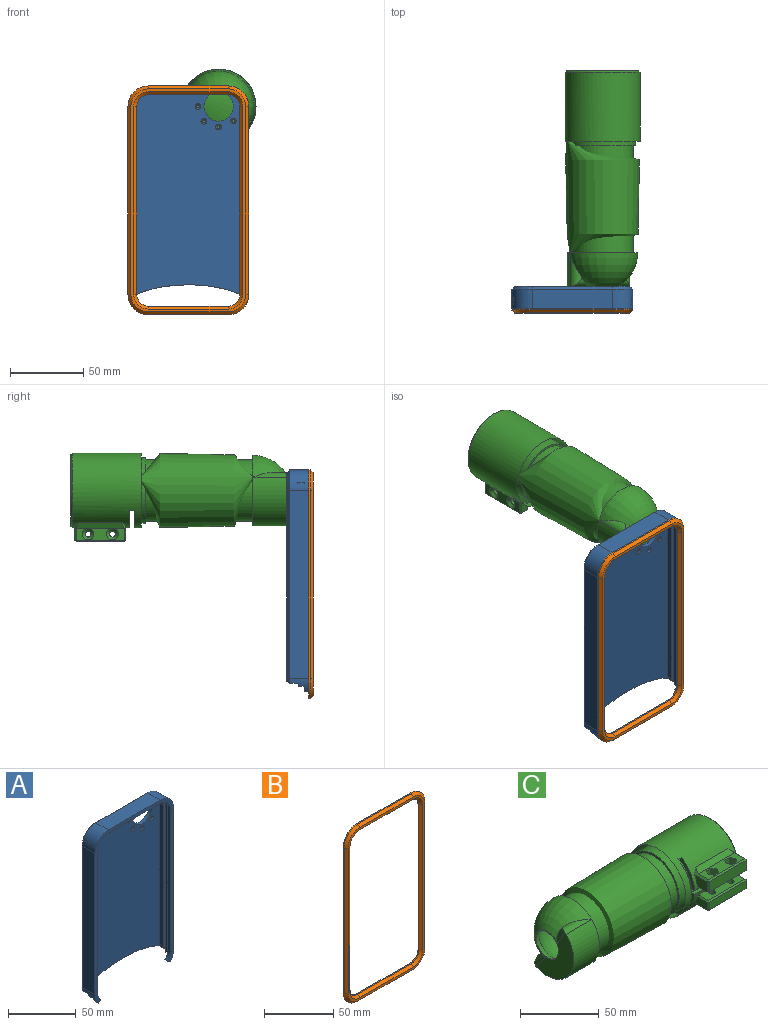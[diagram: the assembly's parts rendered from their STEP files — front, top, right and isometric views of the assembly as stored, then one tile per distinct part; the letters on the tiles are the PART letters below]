
ASSEMBLY  parts=3 mates=1
PART A: 50 faces, bbox 82.3x15x151.3 mm
  f0: cylinder r=14mm len=13mm, axis (0,1,0), area 73mm2, adj f6,f13,f15,f25,f34,f37,f38,f45
  f1: cylinder r=14mm len=13mm, axis (0,1,0), area 73mm2, adj f5,f14,f15,f17,f31,f36,f38,f39
  f2: plane 142.06x78.25mm, normal (0,1,0), area 10255.9mm2, adj f21,f22,f23,f24,f26,f38,f39,f40
  f3: cylinder r=11mm len=4.5mm, axis (0,1,0), area 6.8mm2, adj f16,f27,f35,f38
  f4: cylinder r=11mm len=4.5mm, axis (0,1,0), area 6.8mm2, adj f16,f29,f30,f38
  f5: plane 138.8x4.5mm, normal (-1,0,0), area 623.2mm2, adj f1,f30,f31,f32,f36,f38
  f6: plane 138.8x4.5mm, normal (1,0,0), area 623.2mm2, adj f0,f33,f34,f35,f37,f38
  f7: cylinder r=11mm len=7.84mm, axis (0,1,0), area 26.2mm2, adj f9,f13,f15,f34
  f8: cylinder r=11mm len=7.84mm, axis (0,1,0), area 26.2mm2, adj f12,f14,f15,f31
  f9: plane 128x3mm, normal (1,0,0), area 384mm2, adj f7,f10,f15,f34
  f10: cylinder r=11mm len=12mm, axis (0,1,0), area 182.4mm2, adj f9,f15,f16,f27,f28,f33,f34,f35
  f11: cylinder r=11mm len=12mm, axis (0,1,0), area 182.4mm2, adj f12,f15,f16,f28,f29,f30,f31,f32
  f12: plane 128x3mm, normal (-1,0,0), area 384mm2, adj f8,f11,f15,f31
  f13: extruded ~3x2.77mm, area 9.4mm2, adj f0,f7,f15,f34
  f14: extruded ~3x2.77mm, area 9.4mm2, adj f1,f8,f15,f31
  f15: plane 151.28x82.25mm, normal (0,-1,0), area 1105.1mm2, adj f0,f1,f7,f8,f9,f10,f11,f12
  f16: plane 140.5x76.25mm, normal (0,-1,0), area 9868.2mm2, adj f3,f4,f10,f11,f26,f27,f28,f29
  f17: plane 128x13mm, normal (1,0,0), area 1664mm2, adj f1,f15,f18,f40
  f18: cylinder r=14mm len=14mm, axis (0,1,0), area 285.9mm2, adj f15,f17,f19,f41
  f19: plane 54.25x13mm, normal (0,0,1), area 705.2mm2, adj f15,f18,f20,f42
  f20: cylinder r=14mm len=14mm, axis (0,1,0), area 285.9mm2, adj f15,f19,f25,f43
  f21: cylinder r=1mm len=2mm, axis (0,1,0), area 12.6mm2, adj f2,f49
  f22: cylinder r=1mm len=2mm, axis (0,1,0), area 12.6mm2, adj f2,f48
  f23: cylinder r=1mm len=2mm, axis (0,1,0), area 12.6mm2, adj f2,f47
  f24: cylinder r=1mm len=2mm, axis (0,1,0), area 12.6mm2, adj f2,f46
  f25: plane 128x13mm, normal (-1,0,0), area 1664mm2, adj f0,f15,f20,f44
  f26: cylinder r=10mm len=20mm, axis (0,1,0), area 188.5mm2, adj f2,f16
  f27: plane 128x4.5mm, normal (1,0,0), area 576mm2, adj f3,f10,f16,f35
  f28: plane 54.25x12mm, normal (0,0,-1), area 651mm2, adj f10,f11,f15,f16
  f29: plane 128x4.5mm, normal (-1,0,0), area 576mm2, adj f4,f11,f16,f30
  f30: plane 136.07x3.24mm, normal (0,-1,0), area 256.4mm2, adj f4,f5,f11,f29,f32,f38
  f31: plane 142.59x5.16mm, normal (0,1,0), area 276.4mm2, adj f1,f5,f8,f11,f12,f14,f32
  f32: plane 4.5x3.24mm, normal (0,0,-1), area 14.6mm2, adj f5,f11,f30,f31
  f33: plane 4.5x3.24mm, normal (0,0,-1), area 14.6mm2, adj f6,f10,f34,f35
  f34: plane 142.59x5.16mm, normal (0,1,0), area 276.4mm2, adj f0,f6,f7,f9,f10,f13,f33
  f35: plane 136.07x3.24mm, normal (0,-1,0), area 256.4mm2, adj f3,f6,f10,f27,f33,f38
  f36: plane 2.73x0.73mm, normal (0,1,0), area 1.1mm2, adj f1,f5,f38
  f37: plane 2.73x0.73mm, normal (0,1,0), area 1.1mm2, adj f0,f6,f38
  f38: extruded ~81.46x9.82mm, area 280.9mm2, adj f0,f1,f2,f3,f4,f5,f6,f16
  f39: cone r=14mm half-angle=45deg, axis (0,-1,0), area 7.6mm2, adj f1,f2,f38,f40
  f40: plane 128x2mm, normal (0.71,0.71,0), area 362mm2, adj f2,f17,f39,f41
  f41: cone r=14mm half-angle=45deg, axis (0,-1,0), area 57.8mm2, adj f2,f18,f40,f42
  f42: plane 54.25x2mm, normal (0,0.71,0.71), area 153.4mm2, adj f2,f19,f41,f43
  f43: cone r=14mm half-angle=45deg, axis (0,-1,0), area 57.8mm2, adj f2,f20,f42,f44
  f44: plane 128x2mm, normal (-0.71,0.71,0), area 362mm2, adj f2,f25,f43,f45
  f45: cone r=14mm half-angle=45deg, axis (0,-1,0), area 7.6mm2, adj f0,f2,f38,f44
  f46: cone r=1mm half-angle=45deg, axis (0,-1,0), area 13.3mm2, adj f16,f24
  f47: cone r=1mm half-angle=45deg, axis (0,-1,0), area 13.3mm2, adj f16,f23
  f48: cone r=1mm half-angle=45deg, axis (0,-1,0), area 13.3mm2, adj f16,f22
  f49: cone r=1mm half-angle=45deg, axis (0,-1,0), area 13.3mm2, adj f16,f21
PART B: 34 faces, bbox 82.3x3x156 mm
  f0: cylinder r=8mm len=8mm, axis (0,1,0), area 12.6mm2, adj f1,f15,f17,f26
  f1: plane 128x1mm, normal (-1,0,0), area 128mm2, adj f0,f2,f17,f28
  f2: cylinder r=8mm len=8mm, axis (0,1,0), area 12.6mm2, adj f1,f3,f17,f30
  f3: plane 54.25x1mm, normal (0,0,1), area 54.2mm2, adj f2,f4,f17,f32
  f4: cylinder r=8mm len=8mm, axis (0,1,0), area 12.6mm2, adj f3,f5,f17,f33
  f5: plane 128x1mm, normal (1,0,0), area 128mm2, adj f4,f6,f17,f31
  f6: cylinder r=8mm len=8mm, axis (0,1,0), area 12.6mm2, adj f5,f15,f17,f29
  f7: cylinder r=14mm len=14mm, axis (0,1,0), area 22mm2, adj f8,f14,f17,f23
  f8: plane 54.25x1mm, normal (0,0,-1), area 54.2mm2, adj f7,f9,f17,f25
  f9: cylinder r=14mm len=14mm, axis (0,1,0), area 22mm2, adj f8,f10,f17,f24
  f10: plane 128x1mm, normal (1,0,0), area 128mm2, adj f9,f11,f17,f22
  f11: cylinder r=14mm len=14mm, axis (0,1,0), area 22mm2, adj f10,f12,f17,f20
  f12: plane 54.25x1mm, normal (0,0,1), area 54.2mm2, adj f11,f13,f17,f18
  f13: cylinder r=14mm len=14mm, axis (0,1,0), area 22mm2, adj f12,f14,f17,f19
  f14: plane 128x1mm, normal (-1,0,0), area 128mm2, adj f7,f13,f17,f21
  f15: plane 54.25x1mm, normal (0,0,-1), area 54.2mm2, adj f0,f6,f17,f27
  f16: plane 152x78.25mm, normal (0,-1,0), area 867.2mm2, adj f18,f19,f20,f21,f22,f23,f24,f25
  f17: plane 156x82.25mm, normal (0,1,0), area 2601.7mm2, adj f0,f1,f2,f3,f4,f5,f6,f7
  f18: plane 54.25x2mm, normal (0,-0.71,0.71), area 153.4mm2, adj f12,f16,f19,f20
  f19: cone r=12mm half-angle=45deg, axis (0,1,0), area 57.8mm2, adj f13,f16,f18,f21
  f20: cone r=12mm half-angle=45deg, axis (0,1,0), area 57.8mm2, adj f11,f16,f18,f22
  f21: plane 128x2mm, normal (-0.71,-0.71,0), area 362mm2, adj f14,f16,f19,f23
  f22: plane 128x2mm, normal (0.71,-0.71,0), area 362mm2, adj f10,f16,f20,f24
  f23: cone r=12mm half-angle=45deg, axis (0,1,0), area 57.8mm2, adj f7,f16,f21,f25
  f24: cone r=12mm half-angle=45deg, axis (0,1,0), area 57.8mm2, adj f9,f16,f22,f25
  f25: plane 54.25x2mm, normal (0,-0.71,-0.71), area 153.4mm2, adj f8,f16,f23,f24
  f26: cone r=8mm half-angle=45deg, axis (0,-1,0), area 40mm2, adj f0,f16,f27,f28
  f27: plane 54.25x2mm, normal (0,-0.71,-0.71), area 153.4mm2, adj f15,f16,f26,f29
  f28: plane 128x2mm, normal (-0.71,-0.71,0), area 362mm2, adj f1,f16,f26,f30
  f29: cone r=8mm half-angle=45deg, axis (0,-1,0), area 40mm2, adj f6,f16,f27,f31
  f30: cone r=8mm half-angle=45deg, axis (0,-1,0), area 40mm2, adj f2,f16,f28,f32
  f31: plane 128x2mm, normal (0.71,-0.71,0), area 362mm2, adj f5,f16,f29,f33
  f32: plane 54.25x2mm, normal (0,-0.71,0.71), area 153.4mm2, adj f3,f16,f30,f33
  f33: cone r=8mm half-angle=45deg, axis (0,-1,0), area 40mm2, adj f4,f16,f31,f32
PART C: 82 faces, bbox 147.1x60.6x51.1 mm
  f0: cylinder r=2mm len=4.8mm, axis (0,0,1), area 60.3mm2, adj f23,f69
  f1: cylinder r=2mm len=4.8mm, axis (0,0,1), area 60.3mm2, adj f23,f62
  f2: cylinder r=22.5mm len=51mm, axis (-1,0,0), area 6918.2mm2, adj f4,f10,f12,f13,f14,f15,f16,f17
  f3: cylinder r=25.5mm len=51mm, axis (-1,0,0), area 6443.8mm2, adj f11,f12,f13,f14,f15,f16,f17,f18
  f4: plane 49x48.96mm, normal (1,0,0), area 289.2mm2, adj f2,f12,f18,f29
  f5: revolved ~47.66x44.22mm, area 1755.3mm2, adj f6,f11,f75,f76,f77,f78,f79,f80
  f6: plane 41.7x34.84mm, normal (-1,0,0), area 669.8mm2, adj f5,f7,f74,f77,f78,f79,f80
  f7: cylinder r=10mm len=20mm, axis (-1,0,0), area 12.3mm2, adj f6,f81
  f8: revolved ~42x42mm, area 2399.2mm2, adj f9,f81
  f9: cylinder r=21mm len=73mm, axis (-1,0,0), area 9632.1mm2, adj f8,f10
  f10: plane 45x45mm, normal (1,0,0), area 205mm2, adj f2,f9
  f11: cone r=24mm half-angle=1.1deg, axis (1,0,0), area 11821mm2, adj f3,f5,f74
  f12: plane 40.01x3.01mm, normal (0,0,-1), area 119.8mm2, adj f2,f3,f4,f13,f29
  f13: plane 20x18.82mm, normal (-1,0,0), area 75.9mm2, adj f2,f3,f12,f14
  f14: plane 7.08x3mm, normal (0,0,-1), area 21.2mm2, adj f2,f3,f13,f15
  f15: plane 43x18.87mm, normal (1,0,0), area 160.7mm2, adj f2,f3,f14,f16
  f16: plane 7.08x3mm, normal (0,0,1), area 21.2mm2, adj f2,f3,f15,f17
  f17: plane 20x18.82mm, normal (-1,0,0), area 75.9mm2, adj f2,f3,f16,f18
  f18: plane 40.01x3.01mm, normal (0,0,1), area 119.8mm2, adj f2,f3,f4,f17,f29
  f19: plane 33x8mm, normal (0,-1,0), area 264mm2, adj f45,f46,f50,f51
  f20: plane 11.24x8mm, normal (-1,0,0), area 78mm2, adj f3,f44,f50,f53
  f21: plane 33x9.08mm, normal (0,0,1), area 214.9mm2, adj f42,f44,f45,f56,f57,f58,f59,f60
  f22: plane 11.24x8mm, normal (1,0,0), area 78mm2, adj f3,f42,f46,f47
  f23: plane 33x8.62mm, normal (0,0,-1), area 259.4mm2, adj f0,f1,f3,f47,f51,f53
  f24: plane 33x6mm, normal (0,-1,0), area 198mm2, adj f33,f34,f38,f39
  f25: plane 33x8.42mm, normal (0,0,-1), area 177.2mm2, adj f30,f34,f35,f71,f72,f73
  f26: plane 10.76x6mm, normal (-1,0,0), area 58.2mm2, adj f3,f35,f39,f41
  f27: plane 33x8.74mm, normal (0,0,1), area 263.3mm2, adj f3,f32,f38,f41,f54,f55
  f28: plane 10.76x6mm, normal (1,0,0), area 58.2mm2, adj f3,f30,f32,f33
  f29: cone r=25.5mm half-angle=45deg, axis (-1,0,0), area 217.9mm2, adj f3,f4,f12,f18
  f30: plane 12.59x3.31mm, normal (0.71,0,-0.71), area 20mm2, adj f3,f25,f28,f31,f71
  f31: plane 1x1mm, normal (0.58,-0.58,-0.58), area 0.9mm2, adj f30,f33,f34
  f32: plane 8.9x1mm, normal (0.71,0,0.71), area 12.5mm2, adj f3,f27,f28,f36
  f33: plane 6x1mm, normal (0.71,-0.71,0), area 8.5mm2, adj f24,f28,f31,f36
  f34: plane 33x1mm, normal (0,-0.71,-0.71), area 46.7mm2, adj f24,f25,f31,f37
  f35: plane 12.59x3.31mm, normal (-0.71,0,-0.71), area 20mm2, adj f3,f25,f26,f37,f71
  f36: plane 1x1mm, normal (0.58,-0.58,0.58), area 0.9mm2, adj f32,f33,f38
  f37: plane 1x1mm, normal (-0.58,-0.58,-0.58), area 0.9mm2, adj f34,f35,f39
  f38: plane 33x1mm, normal (0,-0.71,0.71), area 46.7mm2, adj f24,f27,f36,f40
  f39: plane 6x1mm, normal (-0.71,-0.71,0), area 8.5mm2, adj f24,f26,f37,f40
  f40: plane 1x1mm, normal (-0.58,-0.58,0.58), area 0.9mm2, adj f38,f39,f41
  f41: plane 8.9x1mm, normal (-0.71,0,0.71), area 12.5mm2, adj f3,f26,f27,f40
  f42: plane 13.15x3.15mm, normal (0.71,0,0.71), area 20.2mm2, adj f3,f21,f22,f43,f70
  f43: plane 1x1mm, normal (0.58,-0.58,0.58), area 0.9mm2, adj f42,f45,f46
  f44: plane 13.15x3.15mm, normal (-0.71,0,0.71), area 20.2mm2, adj f3,f20,f21,f48,f70
  f45: plane 33x1mm, normal (0,-0.71,0.71), area 46.7mm2, adj f19,f21,f43,f48
  f46: plane 8x1mm, normal (0.71,-0.71,0), area 11.3mm2, adj f19,f22,f43,f49
  f47: plane 8.74x1mm, normal (0.71,0,-0.71), area 12.3mm2, adj f3,f22,f23,f49
  f48: plane 1x1mm, normal (-0.58,-0.58,0.58), area 0.9mm2, adj f44,f45,f50
  f49: plane 1x1mm, normal (0.58,-0.58,-0.58), area 0.9mm2, adj f46,f47,f51
  f50: plane 8x1mm, normal (-0.71,-0.71,0), area 11.3mm2, adj f19,f20,f48,f52
  f51: plane 33x1mm, normal (0,-0.71,-0.71), area 46.7mm2, adj f19,f23,f49,f52
  f52: plane 1x1mm, normal (-0.58,-0.58,-0.58), area 0.9mm2, adj f50,f51,f53
  f53: plane 8.74x1mm, normal (-0.71,0,-0.71), area 12.3mm2, adj f3,f20,f23,f52
  f54: cylinder r=2mm len=6mm, axis (0,0,1), area 75.4mm2, adj f27,f73
  f55: cylinder r=2mm len=6mm, axis (0,0,1), area 75.4mm2, adj f27,f72
  f56: plane 5.2x4.04mm, normal (0,1,0), area 21mm2, adj f21,f57,f61,f62
  f57: plane 5.2x3.5mm, normal (-0.87,0.5,0), area 21mm2, adj f21,f56,f58,f62
  f58: plane 5.2x3.5mm, normal (-0.87,-0.5,0), area 21mm2, adj f21,f57,f59,f62
  f59: plane 5.2x4.04mm, normal (0,-1,0), area 21mm2, adj f21,f58,f60,f62
  f60: plane 5.2x3.5mm, normal (0.87,-0.5,0), area 21mm2, adj f21,f59,f61,f62
  f61: plane 5.2x3.5mm, normal (0.87,0.5,0), area 21mm2, adj f21,f56,f60,f62
  f62: plane 8.08x7.01mm, normal (0,0,1), area 29.9mm2, adj f1,f56,f57,f58,f59,f60,f61
  f63: plane 5.2x4.04mm, normal (0,1,0), area 21mm2, adj f21,f64,f68,f69
  f64: plane 5.2x3.5mm, normal (-0.87,0.5,0), area 21mm2, adj f21,f63,f65,f69
  f65: plane 5.2x3.5mm, normal (-0.87,-0.5,0), area 21mm2, adj f21,f64,f66,f69
  f66: plane 5.2x4.04mm, normal (0,-1,0), area 21mm2, adj f21,f65,f67,f69
  f67: plane 5.2x3.5mm, normal (0.87,-0.5,0), area 21mm2, adj f21,f66,f68,f69
  f68: plane 5.2x3.5mm, normal (0.87,0.5,0), area 21mm2, adj f21,f63,f67,f69
  f69: plane 8.08x7.01mm, normal (0,0,1), area 29.9mm2, adj f0,f63,f64,f65,f66,f67,f68
  f70: plane 33x4mm, normal (0,-0.46,0.89), area 139.5mm2, adj f3,f21,f42,f44
  f71: plane 33x4.11mm, normal (0,-0.48,-0.88), area 144mm2, adj f3,f25,f30,f35
  f72: cone r=2mm half-angle=45deg, axis (0,0,-1), area 53.3mm2, adj f25,f55
  f73: cone r=2mm half-angle=45deg, axis (0,0,-1), area 53.3mm2, adj f25,f54
  f74: cylinder r=24mm len=40.89mm, axis (-1,0,0), area 1508.6mm2, adj f6,f11,f78,f79
  f75: plane 1.56x1.05mm, normal (0,0.8,0.6), area 1mm2, adj f5,f79,f80
  f76: plane 1.56x1.14mm, normal (0,0.87,0.5), area 1mm2, adj f5,f77,f78
  f77: cylinder r=5mm len=14.37mm, axis (0,0.5,-0.87), area 64.4mm2, adj f5,f6,f76,f78
  f78: cylinder r=5mm len=23mm, axis (-1,0,0), area 121.5mm2, adj f5,f6,f74,f76,f77
  f79: cylinder r=5mm len=23mm, axis (-1,0,0), area 121.5mm2, adj f5,f6,f74,f75,f80
  f80: cylinder r=5mm len=13.95mm, axis (0,0.6,-0.8), area 64.4mm2, adj f5,f6,f75,f79
  f81: cone r=12.06mm half-angle=25.8deg, axis (1,0,0), area 328.5mm2, adj f7,f8
PLACE A t=(-36.7,-8.91,15.25)mm fixed
PLACE B t=(-36.7,-23.91,15.25)mm fixed
PLACE C rot(axis=(0.58,0.58,0.58),120deg) t=(-16.07,14.09,79.25)mm
MATE fastened A.f26 <-> C.f11  axis (0,1,0) through (-16.07,-8.91,79.25)mm
